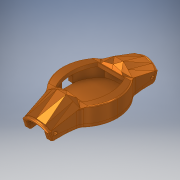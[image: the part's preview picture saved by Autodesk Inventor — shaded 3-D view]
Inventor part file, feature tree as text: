
AUTODESK INVENTOR PART (.ipt)
format: ipt  version: 2019 (Build 230136000, 136)  size: 1,625,600 bytes
history: native  units: mm
features: sketch x22, extrude x17, other x16, projected_geometry x15, plane x10, fillet x8, mirror x3, revolve x2, hole x2, sweep x1, direct_edit x1, move_body x1
ambient origin geometry x8: Origin, YZ Plane, XZ Plane, XY Plane, X Axis, Y Axis, Z Axis, Center Point
bodies: Volumenkörper1 (feature_tree), Volumenkörper2 (feature_tree), Volumenkörper3 (feature_tree), Volumenkörper5 (feature_tree), Volumenkörper8 (feature_tree), Volumenkörper6 (feature_tree), Volumenkörper7 (feature_tree)
feature tree (98):
  other  "Körper verschieben1"
  plane  "Arbeitsebene3"
  other  "Trennen1"
  plane  "Arbeitsebene1"
  sketch  "Skizze2"  dims[d2=90.0deg d3=0.8mm]
  plane  "Arbeitsebene2"
  plane  "Arbeitsebene4"
  other  "Trennen2"
  extrude  "Extrusion3"  Depth=0.8mm
  plane  "Arbeitsebene5"
  sweep  "Sweeping2"
  plane  "Arbeitsebene9"
  other  "Trennen5"
  extrude  "Extrusion4"  Depth=0.8mm TaperAngle=0.0deg
  revolve  "Umdrehung2"
  extrude  "Extrusion5"  Depth=0.45mm
  hole  "Bohrung1"  [1 undecoded]
  other  "Mittelebene"
  plane  "Arbeitsebene7"
  other  "Trennen3"
  mirror  "Spiegeln1"
  other  "Mittelebene_2"
  extrude  "Extrusion6"  Depth=3.5mm TaperAngle=0.0deg
  other  "Kombinieren2"
  fillet  "Rundung1"  Radius=2.094395mm
  fillet  "Rundung2"  Radius=6.0mm
  fillet  "Rundung3"  Radius=2.8mm
  fillet  "Rundung4"  Radius=0.5mm
  sketch  "Skizze19"  dims[d45=2.5mm d46=1.0mm]
  extrude  "Extrusion9"  Depth=0.3mm
  extrude  "Extrusion10"  Depth=1.0mm
  extrude  "Extrusion11"  TaperAngle=0.0deg  [1 undecoded]
  extrude  "Extrusion12"  Depth=12.89mm
  plane  "Arbeitsebene12"
  other  "Trennen6"
  direct_edit  "Direktbearbeitung3"
  extrude  "Extrusion13"  Depth=10.0mm TaperAngle=0.0deg
  extrude  "Extrusion14"  Depth=10.5mm
  extrude  "Extrusion15"  Depth=2.0mm TaperAngle=0.0deg
  mirror  "Spiegeln2"
  revolve  "Umdrehung3"
  plane  "Arbeitsebene14"
  other  "Trennen8"
  extrude  "Extrusion16"  TaperAngle=0.0deg  [1 undecoded]
  fillet  "Rundung6"  Radius=0.5mm
  other  "Kombinieren3"
  fillet  "Rundung7"  Radius=0.5mm
  fillet  "Rundung8"  Radius=1.0mm
  other  "Kombinieren4"
  other  "Kombinieren5"
  other  "Trennen13"
  mirror  "Spiegeln3"
  extrude  "Extrusion17"  Depth=2.0mm
  extrude  "Extrusion18"  Depth=0.872665mm
  fillet  "Rundung9"  [1 undecoded]
  hole  "Bohrung2"  [1 undecoded]
  extrude  "Extrusion19"  Depth=3.0mm
  extrude  "Extrusion20"  Depth=0.5mm TaperAngle=0.0deg
  plane  "Arbeitsebene15"
  extrude  "Extrusion21"  Depth=0.3mm
  sketch  "Skizze6"  dims[d13=-3.141593mm d14=-3.141593mm]
  projected_geometry  "Projizierte Kontur4"
  sketch  "Skizze7"  dims[d15=0.0mm d16=0.8mm d17=0.0mm]
  sketch  "Skizze8"  dims[d20=0.0mm d21=0.0mm d22=0.45mm]
  sketch  "Skizze9"  dims[d24=0.45mm d25=1.1mm]
  projected_geometry  "Projizierte Kontur6"
  sketch  "Skizze10"  dims[d26=1.1mm d27=3.5mm d28=0.0mm d29=2.094395mm d30=6.0mm d31=0.0mm]
  projected_geometry  "Projizierte Kontur7"
  projected_geometry  "Projizierte Kontur8"
  sketch  "Skizze11"  dims[d32=1.0mm d33=6.0mm d34=4.0mm d35=2.0mm d36=90.0deg d37=8.0mm d38=20.594885mm d40=2.8mm d41=0.5mm d42=0.0mm]
  projected_geometry  "Projizierte Kontur9"
  sketch  "Skizze13"  dims[d43=2.8mm d44=0.3mm]
  projected_geometry  "Projizierte Kontur13"
  projected_geometry  "Projizierte Kontur14"
  projected_geometry  "Projizierte Kontur15"
  sketch  "Skizze21"  dims[d47=0.3mm d48=0.0mm]
  sketch  "Skizze23"  dims[d59=15.56mm d60=12.89mm]
  sketch  "Skizze25"  dims[d61=10.0mm d62=0.0mm d63=10.0mm d64=0.0mm]
  projected_geometry  "Projizierte Kontur21"
  sketch  "Skizze26"  dims[d65=11.43mm d66=10.5mm]
  sketch  "Skizze27"  dims[d67=10.0mm d68=0.0mm d69=2.0mm d70=0.0mm]
  sketch  "Skizze29"  dims[d72=-0.5mm d73=0.0mm d74=0.0mm d75=-0.5mm d76=0.5mm d77=0.0mm d78=0.5mm d79=0.0mm d80=1.0mm]
  projected_geometry  "Projizierte Kontur23"
  sketch  "Skizze30"  dims[d81=2.06mm d82=2.0mm]
  projected_geometry  "Projizierte Kontur24"
  sketch  "Skizze33"  dims[d83=0.5mm d84=0.0mm d85=0.872665mm d86=0.0mm d87=0.0mm]
  sketch  "Skizze34"  dims[d89=1.0mm d90=0.3mm]
  projected_geometry  "Projizierte Kontur25"
  sketch  "Skizze35"  dims[d91=0.3mm d93=3.0mm]
  sketch  "Skizze36"  dims[d94=1.55mm d95=0.5mm d96=0.0mm]
  projected_geometry  "Projizierte Kontur26"
  sketch  "Skizze37"  dims[d97=0.953mm d98=0.0mm d99=0.3mm]
  projected_geometry  "Projizierte Kontur27"
  projected_geometry  "Projizierte Kontur28"
  sketch  "Skizze38"  dims[d100=1.4mm d101=1.4mm d102=1.0mm d103=6.0mm d104=4.0mm d105=2.0mm d106=90.0deg d107=2.5mm d108=0.0mm d109=0.953mm d110=0.0mm d111=2.0mm d112=2.0mm d113=0.953mm d114=-7.853982mm d115=4.5mm d116=1.392mm d117=0.0mm d118=0.578mm d119=0.0mm]
  other  "brep_1"
  other  "Volumenkörper1:1"
  move_body  "Verschieben1"
note: 5 required parameter values undecoded (feature->parameter linkage not recoverable at this tier; creation-order binding heuristic only, values carry confidence <= 0.55)
